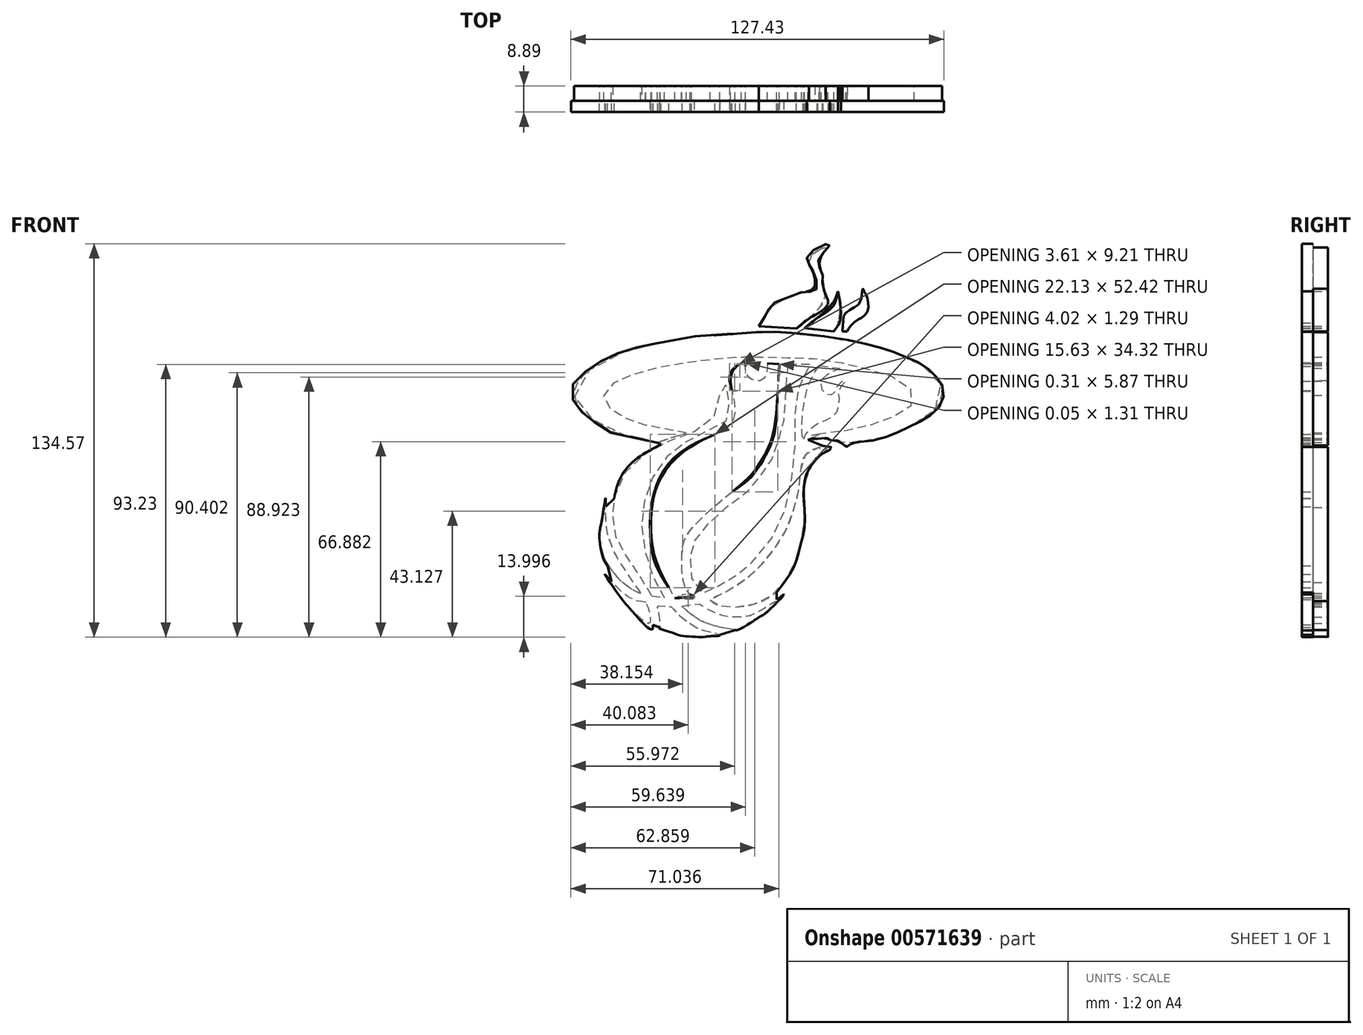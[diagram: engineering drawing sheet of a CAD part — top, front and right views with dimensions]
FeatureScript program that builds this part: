
annotation { "Feature Type Name" : "Feature", "Feature Type Description" : "" }
export const myFeature = defineFeature(function(context is Context, id is Id, definition is map)
    precondition{}
    {
        {
            var Q0;
            Q0=qCreatedBy(makeId("Front.planeOp"),FACE);
            var sketch = newSketch(context, id + "F0", { "sketchPlane" : qUnion([Q0])});
            skFitSpline(sketch, "E0", {"points": [v(-40.4, -51) * mm, v(-42.28, -48.16) * mm, v(-45.11, -43.88) * mm, v(-47.46, -40.38) * mm, v(-49.33, -37.07) * mm, v(-51.14, -32.48) * mm, v(-52.17, -27.72) * mm, v(-52.65, -21.75) * mm, v(-53.8, -26.7) * mm, v(-54.4, -31.16) * mm, v(-54.04, -35.02) * mm, v(-52.53, -39.72) * mm, v(-49.7, -44) * mm, v(-46.02, -47.74) * mm, v(-40.4, -51) * mm]});
            skFitSpline(sketch, "E1", {"points": [v(-38.81, -54.04) * mm, v(-41.59, -53.62) * mm, v(-45.99, -51.26) * mm, v(-50.4, -47.4) * mm, v(-47.01, -52.6) * mm, v(-43.46, -56.75) * mm, v(-37.43, -61.27) * mm, v(-37.13, -58.32) * mm, v(-38.1, -55.18) * mm, v(-38.63, -54.23) * mm], "startDerivative": vector(-30.03, 2.95) * mm, "endDerivative": vector(-9.34, 14.44) * mm});
            skLineSegment(sketch, "E2", {"start": v(-38.81, -54.04) * mm, "end": v(-38.63, -54.23) * mm});
            skFitSpline(sketch, "E3", {"points": [v(-13.42, -65.25) * mm, v(-16.43, -65.7) * mm, v(-19.42, -65.95) * mm, v(-22.92, -65.85) * mm, v(-26.44, -65.46) * mm, v(-30.18, -64.35) * mm, v(-33.8, -62.8) * mm, v(-33.8, -62.42) * mm, v(-33.86, -59.22) * mm, v(-34.73, -55.42) * mm, v(-34.4, -55.4) * mm, v(-30.18, -55.6) * mm, v(-29.85, -55.79) * mm, v(-27.7, -58.08) * mm, v(-25.33, -60.1) * mm, v(-22.7, -61.9) * mm, v(-19.33, -63.56) * mm, v(-13.42, -65.25) * mm]});
            skFitSpline(sketch, "E4", {"points": [v(-26.38, -55.43) * mm, v(-20.42, -54.7) * mm, v(-20.24, -54.7) * mm, v(-18.8, -55.69) * mm, v(-15.1, -57.66) * mm, v(-10.37, -58.98) * mm, v(-5.46, -59) * mm, v(-0.84, -57.71) * mm, v(6.04, -53.67) * mm, v(3.5, -56.58) * mm, v(0, -59.23) * mm, v(-3.71, -61.56) * mm, v(-7.76, -63.57) * mm, v(-8.3, -63.53) * mm, v(-13.42, -62.6) * mm, v(-17.23, -61.53) * mm, v(-21.42, -59.52) * mm, v(-26.01, -55.9) * mm, v(-26.38, -55.43) * mm]});
            skFitSpline(sketch, "E5", {"points": [v(-36.62, -51.9) * mm, v(-38.67, -48.23) * mm, v(-43.01, -41.7) * mm, v(-46.94, -35.65) * mm, v(-48.66, -32.2) * mm, v(-49.86, -26.1) * mm, v(-49.81, -21.84) * mm, v(-48.77, -16.36) * mm, v(-45.76, -9.84) * mm, v(-40.4, -4.46) * mm, v(-32.89, 0) * mm, v(-24.75, 3.42) * mm, v(-18.84, 5.8) * mm, v(-14.25, 11.54) * mm, v(-13.42, 16.68) * mm, v(-11.65, 21.56) * mm, v(-11.15, 17.83) * mm, v(-10.44, 14.82) * mm, v(-10.15, 11.16) * mm, v(-11.65, 7.36) * mm, v(-16.32, 5.07) * mm, v(-22.05, 2.27) * mm, v(-27.5, -0.96) * mm, v(-32.23, -5.26) * mm, v(-36.32, -11.5) * mm, v(-38.83, -18.24) * mm, v(-39.97, -25.2) * mm, v(-39.71, -32.04) * mm, v(-37.82, -40.67) * mm, v(-35.52, -46.77) * mm, v(-32.3, -52.55) * mm], "startDerivative": vector(-64.67, 123.63) * mm, "endDerivative": vector(98.7, -166.28) * mm});
            skLineSegment(sketch, "E6", {"start": v(-36.62, -51.9) * mm, "end": v(-32.3, -52.55) * mm});
            skFitSpline(sketch, "E7", {"points": [v(-28.7, -52.67) * mm, v(-22.98, -52.07) * mm, v(-23.46, -51.46) * mm, v(-24.49, -50.44) * mm, v(-25.33, -48.57) * mm, v(-26.01, -45.86) * mm, v(-26.38, -39.95) * mm, v(-26.01, -34.52) * mm, v(-23.46, -29.45) * mm, v(-11.6, -18.27) * mm, v(-3.29, -11.17) * mm, v(1.99, -3.77) * mm, v(4.93, 4.04) * mm, v(6.24, 15) * mm, v(6.95, 27.29) * mm], "startDerivative": vector(120.86, 3.22) * mm, "endDerivative": vector(6.38, 126.06) * mm});
            skLineSegment(sketch, "E8", {"start": v(2.87, 27.62) * mm, "end": v(6.95, 27.29) * mm});
            skLineSegment(sketch, "E9", {"start": v(9.9, 27.29) * mm, "end": v(17.42, 27.29) * mm});
            skLineSegment(sketch, "E10", {"start": v(20.58, 26.83) * mm, "end": v(27.75, 25.9) * mm});
            skLineSegment(sketch, "E11", {"start": v(-5.95, 27.84) * mm, "end": v(-4.6, 27.84) * mm});
            skFitSpline(sketch, "E12", {"points": [v(2.87, 27.62) * mm, v(2.87, 26.19) * mm, v(2.08, 23.03) * mm, v(-0.65, 21.53) * mm, v(-4.02, 23.68) * mm, v(-4.6, 27.84) * mm], "startDerivative": vector(0.33, -9.26) * mm, "endDerivative": vector(0.82, 19.06) * mm});
            skFitSpline(sketch, "E13", {"points": [v(-5.95, 27.84) * mm, v(-7.82, 26.36) * mm, v(-9.47, 23.68) * mm, v(-9.47, 19.6) * mm, v(-8.82, 16.65) * mm, v(-8.25, 12.92) * mm, v(-8.4, 9.4) * mm, v(-10.26, 6.11) * mm, v(-13.27, 4.1) * mm, v(-17.35, 2.24) * mm, v(-24.24, -1.56) * mm, v(-31.3, -8.12) * mm, v(-35.03, -15.08) * mm, v(-36.6, -22.03) * mm, v(-36.72, -32.04) * mm, v(-34.7, -41.19) * mm, v(-28.7, -52.67) * mm], "startDerivative": vector(-46.7, -32.7) * mm, "endDerivative": vector(72.64, -124.64) * mm});
            skFitSpline(sketch, "E14", {"points": [v(9.9, 27.29) * mm, v(9.5, 25.9) * mm, v(9.38, 23.05) * mm, v(9.3, 20.03) * mm, v(9.03, 15.42) * mm, v(8.78, 10.65) * mm, v(7.94, 5.8) * mm, v(6.74, 1.52) * mm, v(5.47, -2.04) * mm, v(4.08, -5.72) * mm, v(1.32, -9.85) * mm, v(-1.69, -13.65) * mm, v(-4.6, -16.95) * mm, v(-10.43, -21.18) * mm, v(-14.67, -24.9) * mm, v(-18.8, -28.7) * mm, v(-21.33, -32.04) * mm, v(-22.7, -34.73) * mm, v(-23.46, -38.03) * mm, v(-23.46, -40.83) * mm, v(-22.7, -46.77) * mm, v(-19.9, -51.06) * mm, v(-19.22, -50.96) * mm, v(-17.23, -50.13) * mm, v(-14.3, -48.8) * mm, v(-10.47, -46.77) * mm, v(-6.64, -44.1) * mm, v(-3.29, -41.42) * mm, v(2.87, -34.38) * mm, v(7.94, -25.34) * mm, v(10.52, -15.88) * mm, v(12.23, -3.14) * mm, v(12.5, 5.81) * mm, v(12.6, 14.91) * mm, v(13.96, 19.93) * mm, v(17.42, 27.29) * mm], "startDerivative": vector(-25.26, -105.45) * mm, "endDerivative": vector(106.87, 225.1) * mm});
            skFitSpline(sketch, "E15", {"points": [v(-16.7, -53.36) * mm, v(-15.8, -54.17) * mm, v(-14.17, -55.08) * mm, v(-12.45, -55.38) * mm, v(-9.2, -55.69) * mm, v(-4.84, -55.48) * mm, v(0, -54.17) * mm, v(4.7, -51.63) * mm, v(7.73, -48.39) * mm, v(10.37, -44.63) * mm, v(12.9, -39.06) * mm, v(14.43, -33.68) * mm, v(15.44, -27.7) * mm, v(15.44, -20.6) * mm, v(15.34, -16.44) * mm, v(15.64, -13.1) * mm, v(16.66, -9.65) * mm, v(18.69, -6.3) * mm, v(21.22, -3.67) * mm, v(23.55, -1.54) * mm, v(21.02, -1.03) * mm, v(18.38, -1.94) * mm, v(15.44, -4.07) * mm, v(14.43, -6.91) * mm, v(13.92, -11.98) * mm, v(13.2, -17.25) * mm, v(12, -21.72) * mm, v(10.37, -26.69) * mm, v(8.04, -31.45) * mm, v(3.98, -37.43) * mm, v(0.94, -41.09) * mm, v(-2.3, -44.43) * mm, v(-6.67, -47.88) * mm, v(-12.85, -51.33) * mm, v(-16.7, -53.36) * mm]});
            skFitSpline(sketch, "E16", {"points": [v(15.34, 1.65) * mm, v(16.03, 3.44) * mm, v(17.61, 5.09) * mm, v(20.34, 7.17) * mm, v(23.42, 8.39) * mm, v(26, 10.18) * mm, v(27.3, 12.83) * mm, v(27.43, 16.42) * mm, v(27.58, 19.07) * mm, v(29.73, 21.5) * mm, v(27.8, 21) * mm, v(26.29, 18.64) * mm, v(25.43, 17.13) * mm, v(23.85, 16.7) * mm, v(22.06, 17.85) * mm, v(21.27, 20.43) * mm, v(21.91, 22.51) * mm, v(24.2, 24.38) * mm, v(27.75, 25.9) * mm], "startDerivative": vector(11.26, 39.75) * mm, "endDerivative": vector(55.12, 20.78) * mm});
            skFitSpline(sketch, "E17", {"points": [v(20.58, 26.83) * mm, v(19.26, 24.95) * mm, v(17.68, 22.01) * mm, v(16.4, 18.86) * mm, v(15.44, 14.7) * mm, v(14.74, 9.75) * mm, v(14.74, 2.87) * mm, v(15.34, 1.65) * mm], "startDerivative": vector(-11.47, -15.32) * mm, "endDerivative": vector(7.78, -10.07) * mm});
            skFitSpline(sketch, "E18", {"points": [v(0, 40.34) * mm, v(2.21, 43.92) * mm, v(5.08, 47.5) * mm, v(9.96, 50.09) * mm, v(15.4, 51.95) * mm, v(18.7, 53.39) * mm, v(18.85, 57.55) * mm, v(17.42, 61.27) * mm, v(17.85, 64.43) * mm, v(22.72, 67.15) * mm, v(21.86, 65.15) * mm, v(20.71, 61.7) * mm, v(21.58, 57.55) * mm, v(22, 53.82) * mm, v(22.15, 49.08) * mm, v(12.83, 39.48) * mm], "startDerivative": vector(34.05, 55.81) * mm, "endDerivative": vector(-109.9, -88.61) * mm});
            skLineSegment(sketch, "E19", {"start": v(0, 40.34) * mm, "end": v(12.83, 39.48) * mm});
            skFitSpline(sketch, "E20", {"points": [v(27.02, 52.24) * mm, v(25.16, 48.22) * mm, v(15.55, 39.62) * mm], "startDerivative": vector(-3.17, -10.36) * mm, "endDerivative": vector(-18.45, -14.52) * mm});
            skLineSegment(sketch, "E21", {"start": v(15.55, 39.62) * mm, "end": v(25.6, 38.47) * mm});
            skFitSpline(sketch, "E22", {"points": [v(25.6, 38.47) * mm, v(27.17, 41.77) * mm, v(27.58, 48.1) * mm, v(27.02, 52.24) * mm], "startDerivative": vector(6.16, 9.77) * mm, "endDerivative": vector(-2.15, 12.02) * mm});
            skFitSpline(sketch, "E23", {"points": [v(28.54, 38.47) * mm, v(28.74, 42.15) * mm, v(29.34, 44.5) * mm, v(31.9, 46.32) * mm, v(34.7, 48.85) * mm, v(35.48, 53.09) * mm, v(35.9, 52.24) * mm, v(36.72, 50.96) * mm, v(37.22, 49.1) * mm, v(37.38, 46.16) * mm, v(36.2, 44.08) * mm, v(34.53, 42.9) * mm, v(32.41, 41.46) * mm, v(30.65, 39.49) * mm, v(30.22, 38.47) * mm, v(30.22, 38.47) * mm], "startDerivative": vector(2.06, 44.54) * mm, "endDerivative": vector(-7.54, 3.93) * mm});
            skLineSegment(sketch, "E24", {"start": v(28.54, 38.47) * mm, "end": v(30.22, 38.47) * mm});
            skFitSpline(sketch, "E25", {"points": [v(-24.75, 3.83) * mm, v(-30.1, 4.8) * mm, v(-37.93, 6.25) * mm, v(-44.08, 8.18) * mm, v(-49.27, 10.83) * mm, v(-52.28, 13.84) * mm, v(-52.76, 17.46) * mm, v(-49.39, 21.08) * mm, v(-43.6, 23.61) * mm, v(-31.54, 26.87) * mm, v(-21.53, 28.31) * mm, v(-10.56, 29.52) * mm, v(0, 29.76) * mm, v(9.7, 29.52) * mm, v(20.68, 29.04) * mm, v(33.34, 26.63) * mm, v(43.23, 23.85) * mm, v(50.83, 20.11) * mm, v(52.88, 14.57) * mm, v(48.3, 10.47) * mm, v(41.06, 7.45) * mm, v(31.9, 4.92) * mm, v(20.94, 3.42) * mm], "startDerivative": vector(-134.23, 25.02) * mm, "endDerivative": vector(-201.85, -41.2) * mm});
            skFitSpline(sketch, "E26", {"points": [v(20.94, 3.42) * mm, v(17.6, 2.84) * mm, v(17.41, 2.74) * mm, v(16.75, 1.41) * mm, v(17.02, 1.37) * mm, v(17.65, 1.42) * mm, v(17.9, 1.78) * mm, v(18.64, 1.9) * mm, v(21.8, 1.88) * mm, v(23.53, 1.9) * mm, v(24.7, 1.4) * mm, v(26.67, 1) * mm, v(30.07, -0.48) * mm, v(31.59, 0) * mm, v(33.36, 0.59) * mm, v(38.03, 1.25) * mm, v(45.69, 3.42) * mm, v(50.3, 5.4) * mm, v(55.47, 8.04) * mm, v(59.98, 11.5) * mm, v(62.47, 15.9) * mm, v(62.06, 20.47) * mm, v(59.83, 23.56) * mm, v(56.03, 26.7) * mm, v(50.05, 29.7) * mm, v(43.6, 32.18) * mm, v(37.07, 34) * mm, v(28.6, 35.73) * mm, v(10.76, 37.83) * mm, v(0, 38.13) * mm, v(-13.75, 37.34) * mm, v(-21.43, 36.7) * mm, v(-32.39, 34.87) * mm, v(-41.62, 32.85) * mm, v(-51.45, 29.3) * mm, v(-58.85, 24.53) * mm, v(-63.01, 18.65) * mm, v(-61.8, 13.07) * mm, v(-57.74, 9.02) * mm, v(-49.39, 4.1) * mm, v(-40.8, 1.82) * mm, v(-35.12, 0.52) * mm, v(-34.05, 0.73) * mm, v(-24.75, 3.83) * mm], "startDerivative": vector(-229.6, -40.42) * mm, "endDerivative": vector(359.1, 117.94) * mm});
            skSolve(sketch);
        }
        {
            var Q0;
            Q0 = qSketchRegion(id + "F0", true);
            extrude(context, id + "F1", {"entities" : qUnion([Q0]), "depth" : 5.08 * mm, "offsetDistance" : 25.4 * mm});
        }
        {
            var Q0;
            Q0=makeQuery(id+"F1.opExtrude","CAP_FACE",FACE,{"disambiguationData":[OSD([sQuery(id+"F0.wireOp",EDGE,"E7"),sQuery(id+"F0.wireOp",EDGE,"E8"),sQuery(id+"F0.wireOp",EDGE,"E11"),sQuery(id+"F0.wireOp",EDGE,"E12"),sQuery(id+"F0.wireOp",EDGE,"E13")])],"isStart":false});
            var sketch = newSketch(context, id + "F2", { "sketchPlane" : qUnion([Q0])});
            skFitSpline(sketch, "E27.0.0", {"points": [v(-24.75, 3.83) * mm, v(-26.42, 4.15) * mm, v(-30.12, 4.84) * mm, v(-38.02, 6.08) * mm, v(-44, 7.98) * mm, v(-49.32, 10.58) * mm, v(-52.6, 13.53) * mm, v(-53.5, 17.78) * mm, v(-49.25, 21.56) * mm, v(-43.56, 23.77) * mm, v(-31.34, 27.25) * mm, v(-21.67, 28.24) * mm, v(-10.55, 29.75) * mm, v(-0.02, 29.84) * mm, v(9.79, 29.45) * mm, v(20.73, 29.47) * mm, v(33.34, 26.76) * mm, v(42.97, 24.01) * mm, v(51.28, 21.2) * mm, v(54.35, 14.04) * mm, v(48.07, 10.1) * mm, v(41.02, 7.34) * mm, v(31.89, 4.44) * mm, v(24.52, 4.16) * mm, v(20.94, 3.42) * mm]});
            skFitSpline(sketch, "E27.0.1", {"points": [v(20.94, 3.42) * mm, v(19.45, 3.16) * mm, v(17.59, 2.83) * mm, v(17.42, 2.83) * mm, v(16.5, 1.24) * mm, v(17.05, 1.42) * mm, v(17.73, 1.28) * mm, v(17.85, 1.9) * mm, v(18.74, 1.92) * mm, v(21.83, 1.77) * mm, v(23.52, 2.12) * mm, v(24.71, 1.2) * mm, v(26.74, 1.34) * mm, v(30.02, -1.01) * mm, v(31.6, 0.09) * mm, v(33.5, 0.75) * mm, v(38.23, 1.02) * mm, v(45.8, 3.3) * mm, v(50.21, 5.36) * mm, v(55.58, 7.91) * mm, v(60.19, 11.18) * mm, v(63, 15.7) * mm, v(62.44, 20.66) * mm, v(59.86, 23.67) * mm, v(56.1, 27) * mm, v(50, 29.77) * mm, v(43.67, 32.3) * mm, v(36.77, 34.12) * mm, v(28.62, 35.96) * mm, v(10.33, 38.05) * mm, v(0.58, 38.35) * mm, v(-13.95, 37.3) * mm, v(-21.2, 36.9) * mm, v(-32.62, 34.86) * mm, v(-41.51, 33.1) * mm, v(-51.62, 29.64) * mm, v(-58.88, 25.03) * mm, v(-64.13, 19.03) * mm, v(-62.13, 12.61) * mm, v(-57.8, 8.84) * mm, v(-49.47, 3.41) * mm, v(-41.39, 2.11) * mm, v(-35.1, 0.3) * mm, v(-33.98, 0.8) * mm, v(-28.7, 2.53) * mm, v(-24.75, 3.83) * mm]});
            skFitSpline(sketch, "E28.0.0", {"points": [v(12.83, 39.48) * mm, v(16.98, 42.83) * mm, v(23.61, 48.17) * mm, v(21.78, 53.78) * mm, v(21.85, 57.51) * mm, v(20.2, 61.76) * mm, v(21.54, 64.84) * mm, v(24.12, 68.45) * mm, v(16.73, 64.7) * mm, v(17.23, 61.15) * mm, v(19.13, 57.8) * mm, v(19.49, 52.71) * mm, v(15.14, 52.05) * mm, v(9.96, 50.15) * mm, v(4.8, 47.93) * mm, v(2.2, 43.94) * mm, v(0.72, 41.52) * mm, v(0, 40.34) * mm]});
            skLineSegment(sketch, "E28.0.1", {"start": v(0, 40.34) * mm, "end": v(12.83, 39.48) * mm});
            skLineSegment(sketch, "E29.0.0", {"start": v(15.55, 39.62) * mm, "end": v(25.6, 38.47) * mm});
            skFitSpline(sketch, "E29.0.1", {"points": [v(25.6, 38.47) * mm, v(26.2, 39.43) * mm, v(27.6, 41.66) * mm, v(27.76, 48.15) * mm, v(27.25, 50.97) * mm, v(27.02, 52.24) * mm]});
            skFitSpline(sketch, "E29.0.2", {"points": [v(27.02, 52.24) * mm, v(26.63, 50.96) * mm, v(25.58, 47.51) * mm, v(19.43, 42.67) * mm, v(15.55, 39.62) * mm]});
            skFitSpline(sketch, "E30.0.0", {"points": [v(30.22, 38.47) * mm, v(30.22, 38.47) * mm, v(30.2, 38.48) * mm, v(30.65, 39.82) * mm, v(32.35, 41.53) * mm, v(34.51, 42.9) * mm, v(36.32, 43.95) * mm, v(37.72, 46.12) * mm, v(37.23, 49.07) * mm, v(36.88, 51.02) * mm, v(35.87, 52) * mm, v(35.29, 54.2) * mm, v(35.31, 47.96) * mm, v(32, 46.4) * mm, v(28.97, 44.76) * mm, v(28.7, 42.07) * mm, v(28.6, 39.77) * mm, v(28.54, 38.47) * mm]});
            skLineSegment(sketch, "E30.0.1", {"start": v(28.54, 38.47) * mm, "end": v(30.22, 38.47) * mm});
            skLineSegment(sketch, "E31.0.0", {"start": v(27.75, 25.9) * mm, "end": v(20.58, 26.83) * mm});
            skFitSpline(sketch, "E31.0.1", {"points": [v(20.58, 26.83) * mm, v(20.14, 26.25) * mm, v(19.18, 24.97) * mm, v(17.62, 21.96) * mm, v(16.26, 18.9) * mm, v(15.38, 14.5) * mm, v(14.63, 10.06) * mm, v(14.37, 2.9) * mm, v(15.11, 1.94) * mm, v(15.34, 1.65) * mm]});
            skFitSpline(sketch, "E31.0.2", {"points": [v(15.34, 1.65) * mm, v(15.52, 2.27) * mm, v(15.89, 3.58) * mm, v(17.65, 5.11) * mm, v(20.23, 7.45) * mm, v(23.45, 8.2) * mm, v(26.23, 10) * mm, v(27.5, 12.77) * mm, v(27.62, 16.45) * mm, v(26.72, 19.05) * mm, v(31.1, 22.07) * mm, v(27.2, 21.22) * mm, v(26.32, 18.68) * mm, v(25.63, 16.97) * mm, v(23.76, 16.43) * mm, v(21.77, 17.69) * mm, v(21.03, 20.45) * mm, v(21.71, 22.7) * mm, v(24.21, 24.57) * mm, v(26.52, 25.44) * mm, v(27.75, 25.9) * mm]});
            skLineSegment(sketch, "E32.0.0", {"start": v(17.42, 27.29) * mm, "end": v(9.9, 27.29) * mm});
            skFitSpline(sketch, "E32.0.1", {"points": [v(9.9, 27.29) * mm, v(9.76, 26.74) * mm, v(9.36, 25.97) * mm, v(9.4, 22.9) * mm, v(9.32, 20.01) * mm, v(8.99, 15.33) * mm, v(8.92, 10.66) * mm, v(8.02, 5.81) * mm, v(6.82, 1.53) * mm, v(5.41, -2.03) * mm, v(4.3, -5.87) * mm, v(1.36, -9.88) * mm, v(-1.76, -13.67) * mm, v(-4.33, -17.23) * mm, v(-10.7, -21.03) * mm, v(-14.5, -24.9) * mm, v(-18.9, -28.49) * mm, v(-21.37, -31.97) * mm, v(-22.82, -34.61) * mm, v(-23.62, -38.1) * mm, v(-23.4, -40.9) * mm, v(-23.5, -46.64) * mm, v(-20.1, -51.46) * mm, v(-19.2, -50.9) * mm, v(-17.07, -50.1) * mm, v(-14.24, -48.8) * mm, v(-10.4, -46.88) * mm, v(-6.55, -44.04) * mm, v(-3.05, -41.5) * mm, v(3.33, -34.4) * mm, v(8.4, -25.4) * mm, v(10.7, -16.02) * mm, v(12.46, -3.05) * mm, v(12.57, 5.43) * mm, v(12.22, 14.98) * mm, v(13.82, 20.02) * mm, v(16.1, 24.53) * mm, v(17.42, 27.29) * mm]});
            skLineSegment(sketch, "E33.0.0", {"start": v(-4.6, 27.84) * mm, "end": v(-5.95, 27.84) * mm});
            skFitSpline(sketch, "E33.0.1", {"points": [v(-5.95, 27.84) * mm, v(-6.58, 27.4) * mm, v(-7.94, 26.45) * mm, v(-9.92, 23.78) * mm, v(-9.57, 19.5) * mm, v(-8.76, 16.71) * mm, v(-8.17, 12.9) * mm, v(-8.05, 9.37) * mm, v(-10.04, 5.83) * mm, v(-13.33, 4) * mm, v(-17.54, 2.23) * mm, v(-24.58, -1.3) * mm, v(-31.7, -7.72) * mm, v(-35.31, -15.02) * mm, v(-36.9, -22.01) * mm, v(-37.04, -32.27) * mm, v(-35.23, -41.47) * mm, v(-31, -48.74) * mm, v(-28.7, -52.67) * mm]});
            skFitSpline(sketch, "E33.0.2", {"points": [v(-28.7, -52.67) * mm, v(-25.93, -52.6) * mm, v(-22.15, -52.5) * mm, v(-23.57, -51.38) * mm, v(-24.62, -50.5) * mm, v(-25.4, -48.46) * mm, v(-26.2, -45.79) * mm, v(-26.45, -39.86) * mm, v(-26.3, -34.3) * mm, v(-23.88, -28.88) * mm, v(-11.5, -17.88) * mm, v(-3.16, -11.83) * mm, v(2.3, -3.85) * mm, v(5.4, 4) * mm, v(6.3, 15.23) * mm, v(6.74, 23.05) * mm, v(6.95, 27.29) * mm]});
            skLineSegment(sketch, "E33.0.3", {"start": v(6.95, 27.29) * mm, "end": v(2.87, 27.62) * mm});
            skFitSpline(sketch, "E33.0.4", {"points": [v(2.87, 27.62) * mm, v(2.88, 27.2) * mm, v(2.92, 26.15) * mm, v(2.53, 22.72) * mm, v(-0.67, 20.78) * mm, v(-4.78, 23.44) * mm, v(-4.65, 26.36) * mm, v(-4.6, 27.84) * mm]});
            skFitSpline(sketch, "E34.0.0", {"points": [v(-32.3, -52.55) * mm, v(-33.45, -50.62) * mm, v(-35.73, -46.78) * mm, v(-37.97, -40.74) * mm, v(-39.97, -32.03) * mm, v(-40.19, -25.27) * mm, v(-39.04, -18.13) * mm, v(-36.6, -11.4) * mm, v(-32.49, -5.07) * mm, v(-27.66, -0.77) * mm, v(-22.06, 2.28) * mm, v(-16.55, 5.2) * mm, v(-11.15, 6.72) * mm, v(-9.88, 11.12) * mm, v(-10.32, 14.98) * mm, v(-11.35, 17.3) * mm, v(-11.26, 24.07) * mm, v(-13.99, 15.94) * mm, v(-13.41, 11.57) * mm, v(-18.61, 4.96) * mm, v(-24.84, 3.65) * mm, v(-33.02, 0.1) * mm, v(-40.54, -4.13) * mm, v(-46.13, -9.48) * mm, v(-49, -16.17) * mm, v(-49.91, -21.85) * mm, v(-50.05, -26) * mm, v(-48.88, -32.4) * mm, v(-46.96, -35.68) * mm, v(-43.03, -41.78) * mm, v(-38.63, -48.04) * mm, v(-37.22, -50.75) * mm, v(-36.62, -51.9) * mm]});
            skLineSegment(sketch, "E34.0.1", {"start": v(-36.62, -51.9) * mm, "end": v(-32.3, -52.55) * mm});
            skFitSpline(sketch, "E35.0.0", {"points": [v(-40.4, -51) * mm, v(-40.13, -50.8) * mm, v(-42.8, -47.74) * mm, v(-44.97, -43.96) * mm, v(-47.53, -40.39) * mm, v(-49.43, -37.16) * mm, v(-51.29, -32.23) * mm, v(-52.37, -28.55) * mm, v(-52.36, -18.54) * mm, v(-53.9, -27.37) * mm, v(-54.57, -30.98) * mm, v(-54.15, -35.1) * mm, v(-52.82, -39.85) * mm, v(-49.57, -44.22) * mm, v(-46.87, -47.52) * mm, v(-40.8, -51.27) * mm, v(-40.4, -51) * mm]});
            skFitSpline(sketch, "E36.0.0", {"points": [v(-16.7, -53.36) * mm, v(-16.74, -53.64) * mm, v(-15.64, -54.2) * mm, v(-14.2, -55.24) * mm, v(-12.37, -55.37) * mm, v(-9.09, -55.8) * mm, v(-4.75, -55.66) * mm, v(0.04, -54.33) * mm, v(4.9, -51.92) * mm, v(7.77, -48.37) * mm, v(10.56, -44.72) * mm, v(13.08, -39.06) * mm, v(14.48, -33.66) * mm, v(15.71, -27.79) * mm, v(15.45, -20.68) * mm, v(15.26, -16.54) * mm, v(15.55, -13.07) * mm, v(16.47, -9.58) * mm, v(18.68, -6.18) * mm, v(20.74, -3.77) * mm, v(24.97, -1.26) * mm, v(20.61, -0.79) * mm, v(18.47, -1.86) * mm, v(15.02, -3.85) * mm, v(14.32, -6.98) * mm, v(13.95, -12.05) * mm, v(13.36, -17.28) * mm, v(11.99, -21.69) * mm, v(10.46, -26.84) * mm, v(8.2, -31.48) * mm, v(4.06, -37.5) * mm, v(1.01, -41.05) * mm, v(-2.28, -44.58) * mm, v(-6.68, -48.07) * mm, v(-12.15, -51.25) * mm, v(-16.63, -52.8) * mm, v(-16.7, -53.36) * mm]});
            skFitSpline(sketch, "E37.0", {"points": [v(-26.38, -55.43) * mm, v(-25.81, -55.07) * mm, v(-20.33, -54.74) * mm, v(-20.28, -54.64) * mm, v(-18.56, -55.94) * mm, v(-15.08, -57.84) * mm, v(-10.47, -59.26) * mm, v(-5.18, -59.04) * mm, v(-1.34, -58.59) * mm, v(8.46, -51.48) * mm, v(3.14, -57.15) * mm, v(0.04, -59.2) * mm, v(-3.36, -61.47) * mm, v(-7.78, -63.73) * mm, v(-8.27, -63.48) * mm, v(-13.8, -62.65) * mm, v(-17.2, -61.58) * mm, v(-21.46, -59.94) * mm, v(-25.61, -56.05) * mm, v(-26.56, -55.55) * mm, v(-26.38, -55.43) * mm]});
            skFitSpline(sketch, "E38.0", {"points": [v(-13.42, -65.25) * mm, v(-13.39, -65.5) * mm, v(-16.92, -65.7) * mm, v(-19.3, -66.03) * mm, v(-22.96, -65.88) * mm, v(-26.57, -65.59) * mm, v(-29.82, -64.48) * mm, v(-34.07, -62.98) * mm, v(-33.7, -62.33) * mm, v(-33.54, -59.31) * mm, v(-35, -55.2) * mm, v(-34.34, -55.5) * mm, v(-30.05, -55.52) * mm, v(-29.9, -55.76) * mm, v(-27.57, -58.33) * mm, v(-25.44, -60.08) * mm, v(-22.5, -62.03) * mm, v(-20.04, -63.71) * mm, v(-13.47, -64.9) * mm, v(-13.42, -65.25) * mm]});
            skLineSegment(sketch, "E39.0.0", {"start": v(-38.63, -54.23) * mm, "end": v(-38.81, -54.04) * mm});
            skFitSpline(sketch, "E39.0.1", {"points": [v(-38.81, -54.04) * mm, v(-39.72, -53.95) * mm, v(-41.84, -53.74) * mm, v(-45.72, -52.04) * mm, v(-52.64, -44.62) * mm, v(-46.4, -53.57) * mm, v(-44.26, -56.08) * mm, v(-36.55, -63.45) * mm, v(-37.02, -58.03) * mm, v(-37.98, -55.25) * mm, v(-38.46, -54.5) * mm, v(-38.63, -54.23) * mm]});
            skLineSegment(sketch, "E40", {"start": v(-34.76, 0.52) * mm, "end": v(-33.2, -0.16) * mm});
            skLineSegment(sketch, "E41", {"start": v(15.34, 1.65) * mm, "end": v(16.77, 1.37) * mm});
            skLineSegment(sketch, "E42", {"start": v(16.77, 1.37) * mm, "end": v(23.1, -1.2) * mm});
            skLineSegment(sketch, "E43", {"start": v(6.05, -50.38) * mm, "end": v(6.05, -53.79) * mm});
            skLineSegment(sketch, "E44", {"start": v(-7.71, -63.56) * mm, "end": v(-13.42, -65.24) * mm});
            skLineSegment(sketch, "E45", {"start": v(-37.67, -61.3) * mm, "end": v(-33.83, -62.77) * mm});
            skLineSegment(sketch, "E46", {"start": v(-50.32, -47.4) * mm, "end": v(-51.8, -41.02) * mm});
            skLineSegment(sketch, "E47", {"start": v(-52.7, -21.77) * mm, "end": v(-49.3, -18.45) * mm});
            skLineSegment(sketch, "E48", {"start": v(0, 40.34) * mm, "end": v(-9.1, 37.65) * mm});
            skLineSegment(sketch, "E49", {"start": v(27.02, 52.24) * mm, "end": v(12.83, 39.48) * mm});
            skLineSegment(sketch, "E50", {"start": v(27.02, 52.24) * mm, "end": v(28.54, 38.47) * mm});
            skLineSegment(sketch, "E51", {"start": v(30.22, 38.47) * mm, "end": v(42.24, 32.61) * mm});
            skSolve(sketch);
        }
        {
            var Q0;
            Q0 = qSketchRegion(id + "F2", true);
            var Q1;
            Q1=makeQuery(id+"F2.imprint","IMPRINT",FACE,{"disambiguationData":[TD([[makeQuery(id+"F2.imprint","IMPRINT",EDGE,{"derivedFrom":sQuery(id+"F2.wireOp",EDGE,"E32.0.0")}),1.0]])]});
            var Q2;
            Q2=makeQuery(id+"F2.imprint","IMPRINT",FACE,{"disambiguationData":[TD([[makeQuery(id+"F2.imprint","IMPRINT",EDGE,{"derivedFrom":sQuery(id+"F2.wireOp",EDGE,"E31.0.0")}),1.0]])]});
            var Q3;
            Q3=makeQuery(id+"F2.imprint","IMPRINT",FACE,{"disambiguationData":[TD([[makeQuery(id+"F2.imprint","IMPRINT",EDGE,{"derivedFrom":sQuery(id+"F2.wireOp",EDGE,"E33.0.0")}),-1.0]])]});
            extrude(context, id + "F3", {"entities" : qUnion([Q0, Q1, Q2, Q3]), "depth" : 3.8 * mm, "offsetDistance" : 25.4 * mm});
        }
    });
